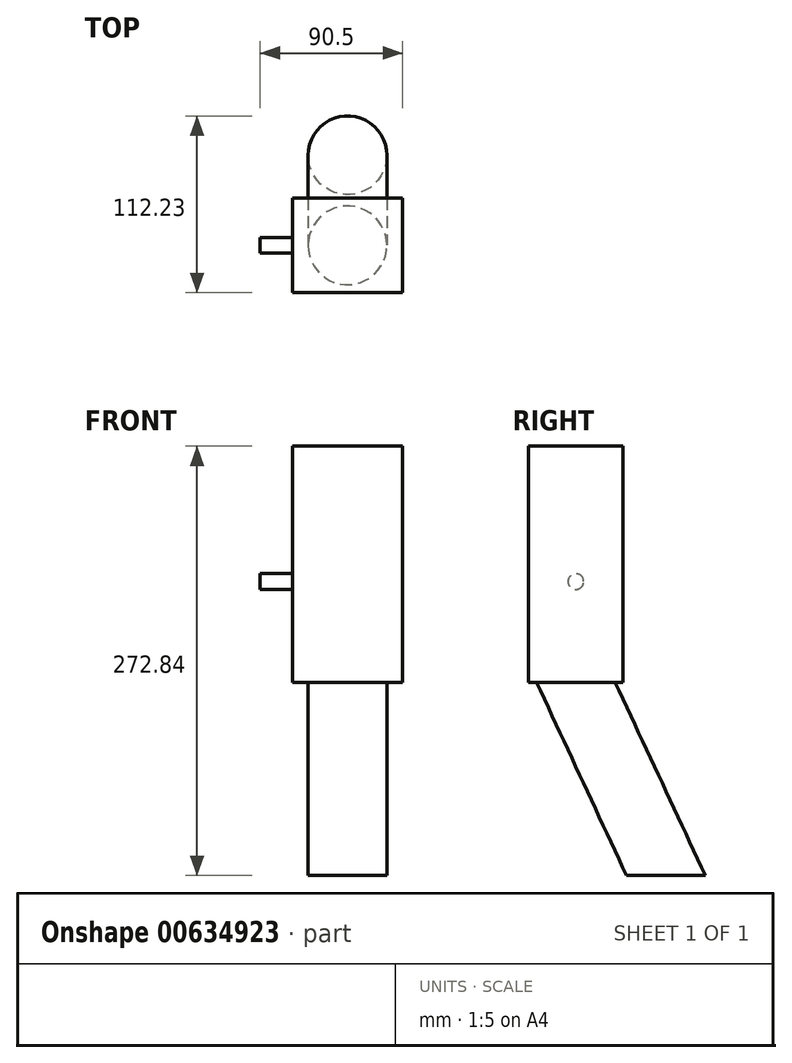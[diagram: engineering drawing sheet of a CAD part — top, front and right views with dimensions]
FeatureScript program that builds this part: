
annotation { "Feature Type Name" : "Feature", "Feature Type Description" : "" }
export const myFeature = defineFeature(function(context is Context, id is Id, definition is map)
    precondition{}
    {
        {
            var Q0;
            Q0=qCreatedBy(makeId("Top.planeOp"),FACE);
            var sketch = newSketch(context, id + "F0", { "sketchPlane" : qUnion([Q0])});
            skLineSegment(sketch, "E0.bottom", {"start": v(0, 0) * mm, "end": v(70, 0) * mm});
            skLineSegment(sketch, "E0.top", {"start": v(0, 60) * mm, "end": v(70, 60) * mm});
            skLineSegment(sketch, "E0.left", {"start": v(0, 0) * mm, "end": v(0, 60) * mm});
            skLineSegment(sketch, "E0.right", {"start": v(70, 0) * mm, "end": v(70, 60) * mm});
            skSolve(sketch);
        }
        {
            var Q0;
            Q0 = qSketchRegion(id + "F0", true);
            extrude(context, id + "F1", {"entities" : qUnion([Q0]), "depth" : 150 * mm, "offsetDistance" : 25 * mm});
        }
        {
            var Q0;
            Q0=makeQuery(id+"F1.opExtrude","SWEPT_FACE",FACE,{"disambiguationData":[OSD([sQuery(id+"F0.wireOp",EDGE,"E0.right")])]});
            cPlane(context, id + "F2", {"entities" : qUnion([Q0]), "cplaneType" : CPlaneType.OFFSET, "offset" : 35 * mm, "oppositeDirection" : true, "width" : 150 * mm, "height" : 150 * mm});
        }
        {
            var Q0;
            Q0=makeQuery(id+"F1.opExtrude","CAP_FACE",FACE,{"disambiguationData":[OSD([sQuery(id+"F0.wireOp",EDGE,"E0.bottom"),sQuery(id+"F0.wireOp",EDGE,"E0.top"),sQuery(id+"F0.wireOp",EDGE,"E0.left"),sQuery(id+"F0.wireOp",EDGE,"E0.right")])],"isStart":true});
            var sketch = newSketch(context, id + "F3", { "sketchPlane" : qUnion([Q0])});
            skCircle(sketch, "E1", {"center": v(35, -30) * mm, "radius": 25 * mm});
            skPoint(sketch, "E1.centerSnap0", {"position": v(70, -30) * mm});
            skSolve(sketch);
        }
        {
            var Q0;
            Q0=qCreatedBy(id+"F2.planeOp",FACE);
            var sketch = newSketch(context, id + "F4", { "sketchPlane" : qUnion([Q0])});
            skLineSegment(sketch, "E2", {"start": v(29.85, 0) * mm, "end": v(87.08, -122.84) * mm});
            skSolve(sketch);
        }
        {
            var Q0;
            Q0=makeQuery(id+"F3.imprint","IMPRINT",FACE,{"disambiguationData":[TD([[makeQuery(id+"F3.imprint","IMPRINT",EDGE,{"derivedFrom":sQuery(id+"F3.wireOp",EDGE,"E1")}),1.0]])]});
            var Q1;
            Q1=sQuery(id+"F4.wireOp",EDGE,"E2");
            sweep(context, id + "F5", {"operationType" : NewBodyOperationType.ADD, "profiles" : qUnion([Q0]), "path" : qUnion([Q1])});
        }
        {
            var Q0;
            Q0=makeQuery(id+"F1.opExtrude","SWEPT_FACE",FACE,{"disambiguationData":[OSD([sQuery(id+"F0.wireOp",EDGE,"E0.left")])]});
            var sketch = newSketch(context, id + "F6", { "sketchPlane" : qUnion([Q0])});
            skCircle(sketch, "E3", {"center": v(-30, 63.93) * mm, "radius": 5 * mm});
            skSolve(sketch);
        }
        {
            var Q0;
            Q0 = qSketchRegion(id + "F6", true);
            extrude(context, id + "F7", {"entities" : qUnion([Q0]), "operationType" : NewBodyOperationType.ADD, "depth" : 20.5 * mm, "offsetDistance" : 25 * mm});
        }
    });
